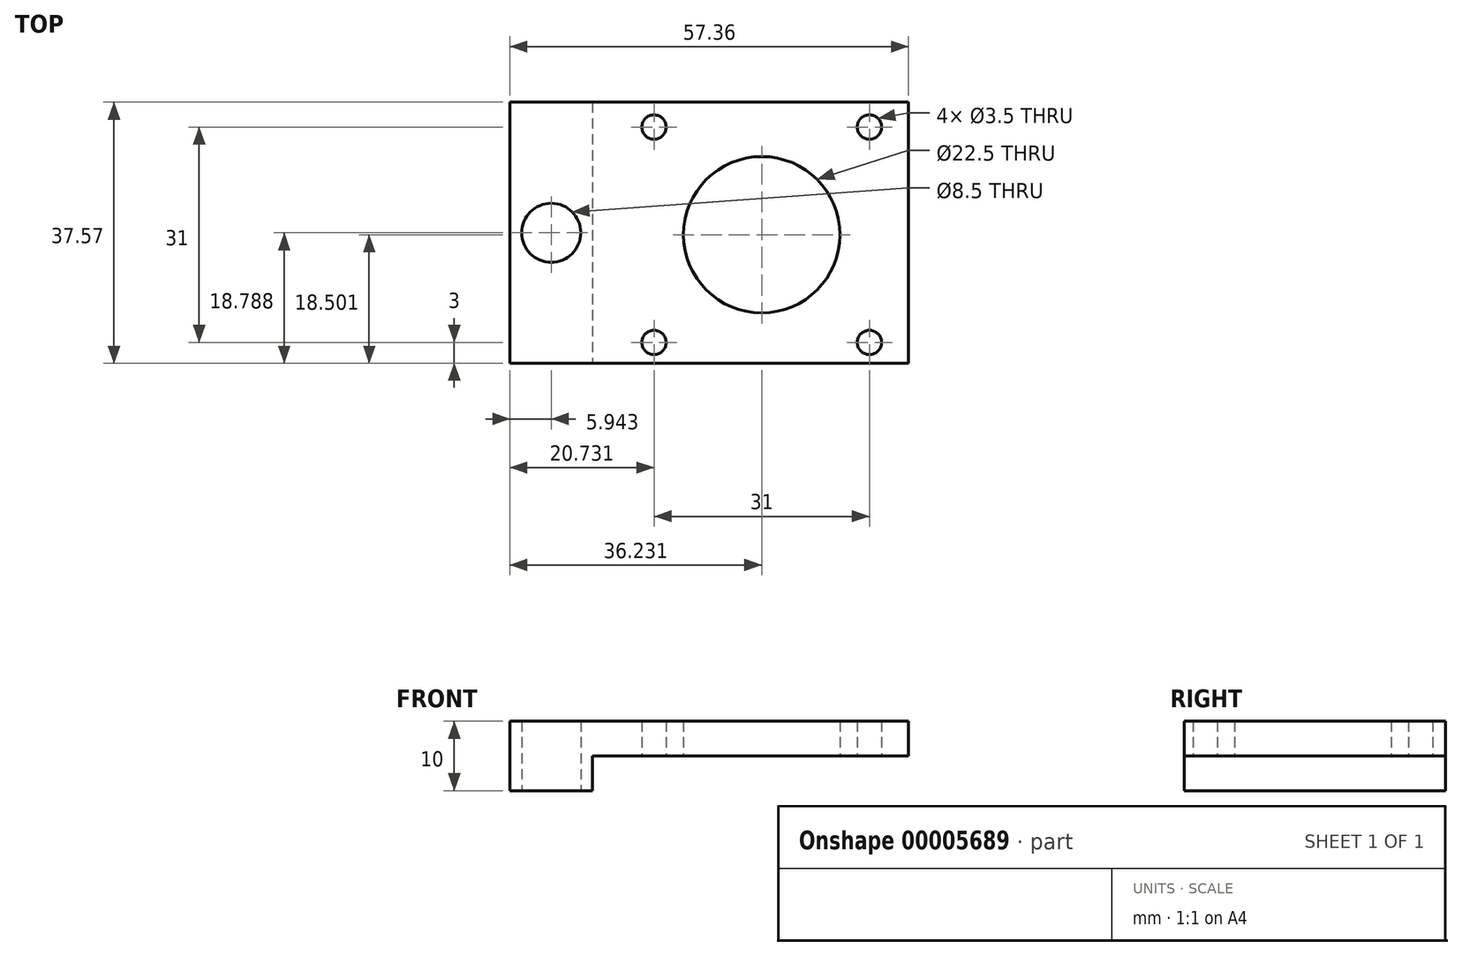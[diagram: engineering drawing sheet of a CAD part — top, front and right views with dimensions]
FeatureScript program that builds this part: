
annotation { "Feature Type Name" : "Feature", "Feature Type Description" : "" }
export const myFeature = defineFeature(function(context is Context, id is Id, definition is map)
    precondition{}
    {
        {
            var Q0;
            Q0=qCreatedBy(makeId("Top.planeOp"),FACE);
            var sketch = newSketch(context, id + "F0", { "sketchPlane" : qUnion([Q0])});
            skLineSegment(sketch, "E0.bottom", {"start": v(19.17, -14.77) * mm, "end": v(-38.2, -14.77) * mm});
            skLineSegment(sketch, "E0.top", {"start": v(19.17, 22.8) * mm, "end": v(-38.2, 22.8) * mm});
            skLineSegment(sketch, "E0.left", {"start": v(19.17, -14.77) * mm, "end": v(19.17, 22.8) * mm});
            skLineSegment(sketch, "E0.right", {"start": v(-38.2, -14.77) * mm, "end": v(-38.2, 22.8) * mm});
            skCircle(sketch, "E1", {"center": v(-17.46, 19.23) * mm, "radius": 1.75 * mm});
            skCircle(sketch, "E2", {"center": v(13.54, 19.23) * mm, "radius": 1.75 * mm});
            skCircle(sketch, "E3", {"center": v(13.54, -11.77) * mm, "radius": 1.75 * mm});
            skCircle(sketch, "E4", {"center": v(-17.46, -11.77) * mm, "radius": 1.75 * mm});
            skCircle(sketch, "E5", {"center": v(-1.96, 3.73) * mm, "radius": 11.25 * mm});
            skLineSegment(sketch, "E6", {"start": v(-26.3, 22.8) * mm, "end": v(-26.3, -14.77) * mm});
            skCircle(sketch, "E7", {"center": v(-32.25, 4.02) * mm, "radius": 4.25 * mm});
            skLineSegment(sketch, "E8", {"start": v(-38.2, 4.02) * mm, "end": v(-26.3, 4.02) * mm, "construction": true});
            skSolve(sketch);
        }
        {
            var Q0;
            {var subQ1=sQuery(id+"F0.wireOp",EDGE,"E0.left");Q0=makeQuery(id+"F0.imprint","IMPRINT",FACE,{"disambiguationData":[TD([[makeQuery(id+"F0.imprint","IMPRINT",EDGE,{"derivedFrom":subQ1}),1.0]])]});}
            extrude(context, id + "F1", {"entities" : qUnion([Q0]), "depth" : 5 * mm});
        }
        {
            var Q0;
            {var subQ1=sQuery(id+"F0.wireOp",EDGE,"E0.right");Q0=makeQuery(id+"F0.imprint","IMPRINT",FACE,{"disambiguationData":[TD([[makeQuery(id+"F0.imprint","IMPRINT",EDGE,{"derivedFrom":subQ1}),-1.0]])]});}
            extrude(context, id + "F2", {"entities" : qUnion([Q0]), "operationType" : NewBodyOperationType.ADD, "endBound" : BoundingType.SYMMETRIC, "depth" : 10 * mm});
        }
    });
